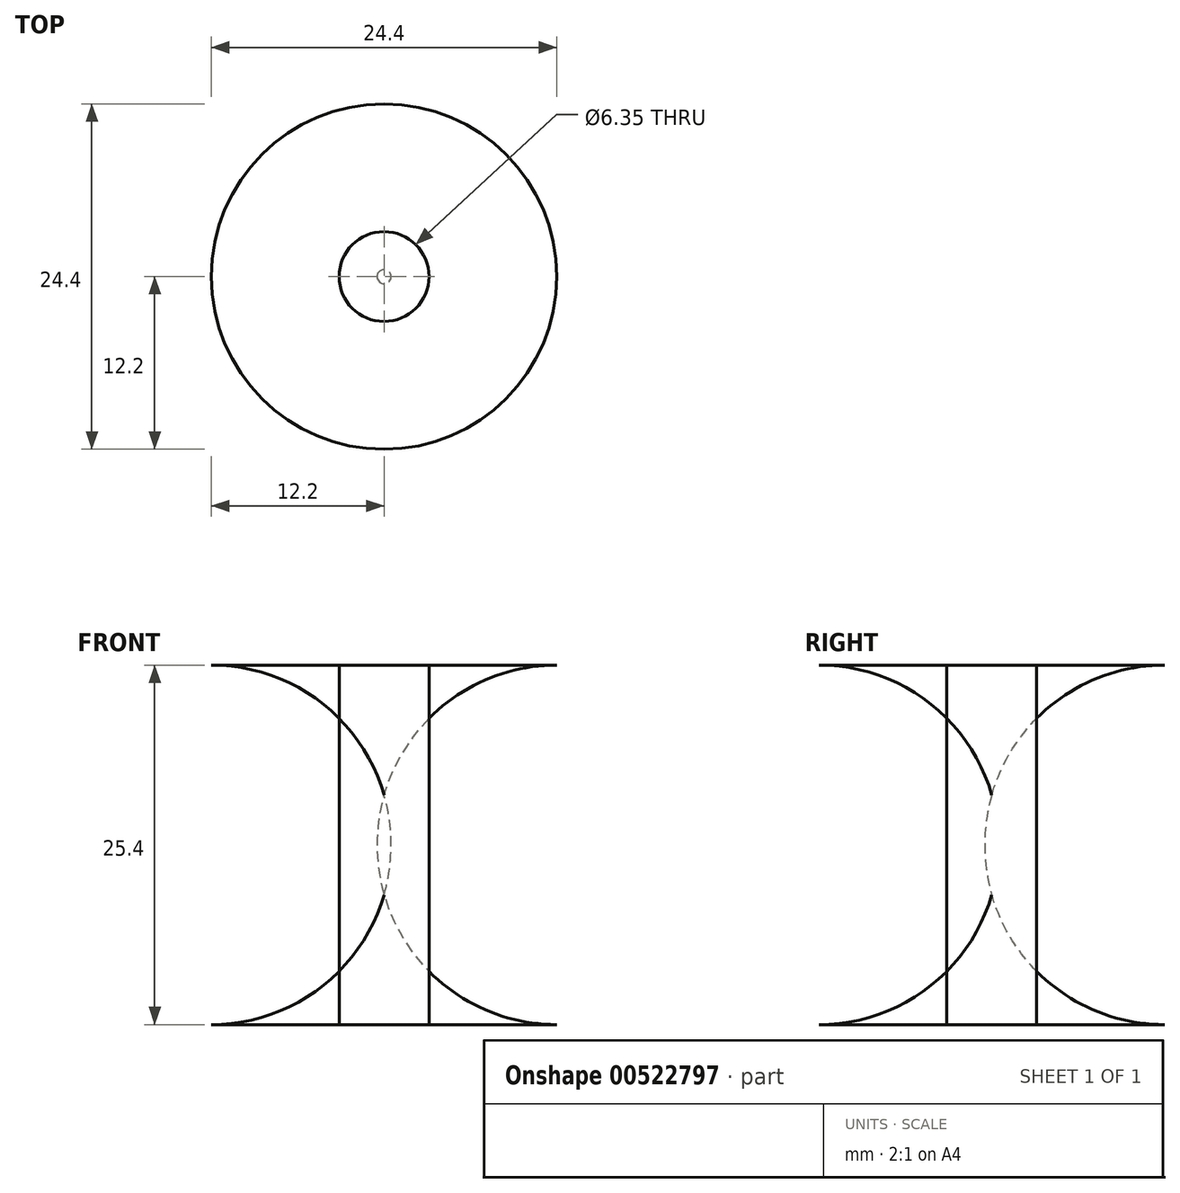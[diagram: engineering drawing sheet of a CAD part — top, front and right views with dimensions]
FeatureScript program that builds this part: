
annotation { "Feature Type Name" : "Feature", "Feature Type Description" : "" }
export const myFeature = defineFeature(function(context is Context, id is Id, definition is map)
    precondition{}
    {
        {
            var Q0;
            Q0=qCreatedBy(makeId("Top.planeOp"),FACE);
            var sketch = newSketch(context, id + "F0", { "sketchPlane" : qUnion([Q0])});
            skCircle(sketch, "E0", {"center": v(0, 0) * mm, "radius": 24.9 * mm});
            skSolve(sketch);
        }
        {
            var Q0;
            Q0 = qSketchRegion(id + "F0", true);
            extrude(context, id + "F1", {"entities" : qUnion([Q0]), "depth" : 25.4 * mm, "offsetDistance" : 25.4 * mm});
        }
        {
            var Q0;
            Q0=makeQuery(id+"F1.opExtrude","CAP_EDGE",EDGE,{"disambiguationData":[OSD([sQuery(id+"F0.wireOp",EDGE,"E0")])],"isStart":true});
            var Q1;
            Q1=makeQuery(id+"F1.opExtrude","CAP_EDGE",EDGE,{"disambiguationData":[OSD([sQuery(id+"F0.wireOp",EDGE,"E0")])],"isStart":false});
            fillet(context, id + "F2", {"entities" : qUnion([Q0, Q1]), "radius" : 12.7 * mm, "tangentPropagation" : true, "allowEdgeOverflow" : false});
        }
        {
            var Q0;
            Q0=makeQuery(id+"F1.opExtrude","CAP_FACE",FACE,{"disambiguationData":[OSD([sQuery(id+"F0.wireOp",EDGE,"E0")])],"isStart":false});
            var sketch = newSketch(context, id + "F3", { "sketchPlane" : qUnion([Q0])});
            skCircle(sketch, "E1", {"center": v(0, 0) * mm, "radius": 3.18 * mm});
            skSolve(sketch);
        }
        {
            var Q0;
            Q0=makeQuery(id+"F3.imprint","IMPRINT",FACE,{"disambiguationData":[TD([[makeQuery(id+"F3.imprint","IMPRINT",EDGE,{"derivedFrom":sQuery(id+"F3.wireOp",EDGE,"E1")}),1.0]])]});
            var Q1;
            Q1=sQuery(id+"F3.wireOp",EDGE,"E1");
            extrude(context, id + "F4", {"entities" : qUnion([Q0]), "operationType" : NewBodyOperationType.REMOVE, "surfaceEntities" : qUnion([Q1]), "endBound" : BoundingType.THROUGH_ALL, "oppositeDirection" : true, "depth" : 25.4 * mm, "offsetDistance" : 25.4 * mm});
        }
    });
